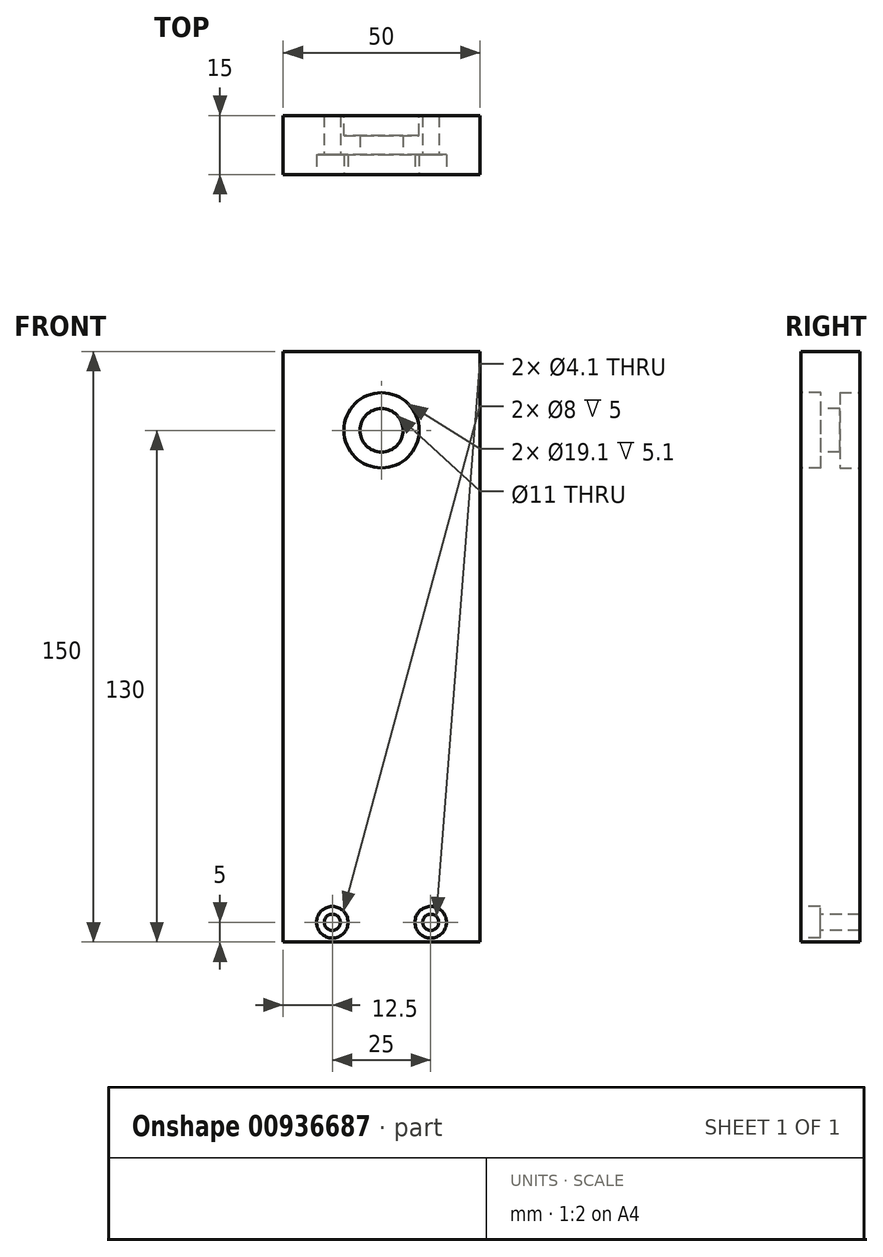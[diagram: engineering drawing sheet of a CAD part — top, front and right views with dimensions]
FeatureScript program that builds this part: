
annotation { "Feature Type Name" : "Feature", "Feature Type Description" : "" }
export const myFeature = defineFeature(function(context is Context, id is Id, definition is map)
    precondition{}
    {
        {
            var Q0;
            Q0=qCreatedBy(makeId("Right.planeOp"),FACE);
            var sketch = newSketch(context, id + "F0", { "sketchPlane" : qUnion([Q0])});
            skLineSegment(sketch, "E0.bottom", {"start": v(0, 0) * mm, "end": v(-15, 0) * mm});
            skLineSegment(sketch, "E0.top", {"start": v(0, 150) * mm, "end": v(-15, 150) * mm});
            skLineSegment(sketch, "E0.left", {"start": v(0, 0) * mm, "end": v(0, 150) * mm});
            skLineSegment(sketch, "E0.right", {"start": v(-15, 0) * mm, "end": v(-15, 150) * mm});
            skSolve(sketch);
        }
        {
            var Q0;
            Q0=makeQuery(id+"F0.imprint","IMPRINT",FACE,{"disambiguationData":[TD([[makeQuery(id+"F0.imprint","IMPRINT",EDGE,{"derivedFrom":sQuery(id+"F0.wireOp",EDGE,"E0.bottom")}),-1.0]])]});
            extrude(context, id + "F1", {"entities" : qUnion([Q0]), "depth" : 50 * mm, "offsetDistance" : 25 * mm});
        }
        {
            var Q0;
            Q0=makeQuery(id+"F1.opExtrude","SWEPT_FACE",FACE,{"disambiguationData":[OSD([sQuery(id+"F0.wireOp",EDGE,"E0.right")])]});
            var sketch = newSketch(context, id + "F2", { "sketchPlane" : qUnion([Q0])});
            skCircle(sketch, "E1", {"center": v(12.5, 5) * mm, "radius": 4 * mm});
            skCircle(sketch, "E2", {"center": v(37.5, 5) * mm, "radius": 4 * mm});
            skCircle(sketch, "E3", {"center": v(12.5, 5) * mm, "radius": 2.05 * mm});
            skCircle(sketch, "E4", {"center": v(37.5, 5) * mm, "radius": 2.05 * mm});
            skCircle(sketch, "E5", {"center": v(25, 130) * mm, "radius": 5.5 * mm});
            skCircle(sketch, "E6", {"center": v(25, 130) * mm, "radius": 9.55 * mm});
            skSolve(sketch);
        }
        {
            var Q0;
            Q0=makeQuery(id+"F2.imprint","IMPRINT",FACE,{"disambiguationData":[TD([[makeQuery(id+"F2.imprint","IMPRINT",EDGE,{"derivedFrom":sQuery(id+"F2.wireOp",EDGE,"E5")}),1.0]])]});
            var Q1;
            Q1=makeQuery(id+"F2.imprint","IMPRINT",FACE,{"disambiguationData":[TD([[makeQuery(id+"F2.imprint","IMPRINT",EDGE,{"derivedFrom":sQuery(id+"F2.wireOp",EDGE,"E3")}),1.0]])]});
            var Q2;
            Q2=makeQuery(id+"F2.imprint","IMPRINT",FACE,{"disambiguationData":[TD([[makeQuery(id+"F2.imprint","IMPRINT",EDGE,{"derivedFrom":sQuery(id+"F2.wireOp",EDGE,"E4")}),1.0]])]});
            extrude(context, id + "F3", {"entities" : qUnion([Q0, Q1, Q2]), "operationType" : NewBodyOperationType.REMOVE, "endBound" : BoundingType.UP_TO_NEXT, "oppositeDirection" : true, "depth" : 25 * mm, "offsetDistance" : 25 * mm});
        }
        {
            var Q0;
            Q0=makeQuery(id+"F2.imprint","IMPRINT",FACE,{"disambiguationData":[TD([[makeQuery(id+"F2.imprint","IMPRINT",EDGE,{"derivedFrom":sQuery(id+"F2.wireOp",EDGE,"E1")}),1.0]])]});
            var Q1;
            Q1=makeQuery(id+"F2.imprint","IMPRINT",FACE,{"disambiguationData":[TD([[makeQuery(id+"F2.imprint","IMPRINT",EDGE,{"derivedFrom":sQuery(id+"F2.wireOp",EDGE,"E2")}),1.0]])]});
            extrude(context, id + "F4", {"entities" : qUnion([Q0, Q1]), "operationType" : NewBodyOperationType.REMOVE, "oppositeDirection" : true, "depth" : 5 * mm, "offsetDistance" : 25 * mm});
        }
        {
            var Q0;
            Q0=makeQuery(id+"F2.imprint","IMPRINT",FACE,{"disambiguationData":[TD([[makeQuery(id+"F2.imprint","IMPRINT",EDGE,{"derivedFrom":sQuery(id+"F2.wireOp",EDGE,"E5")}),-1.0]])]});
            extrude(context, id + "F5", {"entities" : qUnion([Q0]), "operationType" : NewBodyOperationType.REMOVE, "oppositeDirection" : true, "depth" : 5.1 * mm, "offsetDistance" : 25 * mm});
        }
        {
            var Q0;
            Q0=makeQuery(id+"F1.opExtrude","SWEPT_FACE",FACE,{"disambiguationData":[OSD([sQuery(id+"F0.wireOp",EDGE,"E0.left")])]});
            var sketch = newSketch(context, id + "F6", { "sketchPlane" : qUnion([Q0])});
            skCircle(sketch, "E7", {"center": v(-25, 130) * mm, "radius": 9.55 * mm});
            skSolve(sketch);
        }
        {
            var Q0;
            Q0=makeQuery(id+"F6.imprint","IMPRINT",FACE,{"disambiguationData":[TD([[makeQuery(id+"F6.imprint","IMPRINT",EDGE,{"derivedFrom":sQuery(id+"F6.wireOp",EDGE,"E7")}),1.0]])]});
            extrude(context, id + "F7", {"entities" : qUnion([Q0]), "operationType" : NewBodyOperationType.REMOVE, "oppositeDirection" : true, "depth" : 5.1 * mm, "offsetDistance" : 25 * mm});
        }
    });
